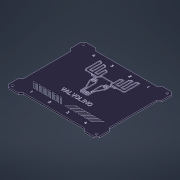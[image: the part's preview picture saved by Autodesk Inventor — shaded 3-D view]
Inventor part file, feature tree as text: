
AUTODESK INVENTOR PART (.ipt)
format: ipt  version: 2021.3 (Build 253353000, 353)  size: 1,772,032 bytes
history: native  units: mm
features: sketch x5, projected_geometry x4, extrude x2, mirror x2, chamfer x1, emboss x1, other x1, hole x1
ambient origin geometry x8: Origin, YZ Plane, XZ Plane, XY Plane, X Axis, Y Axis, Z Axis, Center Point
bodies: Solid1 (feature_tree)
feature tree (17):
  extrude  "Extrusion1"  Depth=110.0mm
  extrude  "Extrusion2"  Depth=2.0mm
  mirror  "Mirror1"
  chamfer  "Chamfer1"  Distance=2.0mm
  emboss  "Emboss1"
  other  "Grill1"
  mirror  "Mirror2"
  hole  "Hole1"  [1 undecoded]
  sketch  "Sketch1"  dims[d0=130.0mm d1=110.0mm]
  sketch  "Sketch2"  dims[d2=4.0mm d3=15.0mm d4=2.0mm d5=0.0mm]
  projected_geometry  "Projected Loop1"
  sketch  "Sketch3"  dims[d74=10.0mm d75=4.0mm]
  projected_geometry  "Projected Loop2"
  sketch  "Sketch4"  dims[d76=2.0mm]
  projected_geometry  "Projected Loop3"
  sketch  "Sketch5"  dims[d77=4.0mm d78=4.0mm d79=4.0mm d80=135.0deg d81=19.0mm d82=4.0mm d83=4.0mm d85=2.0mm d86=8.0mm d87=2.0mm d89=2.0mm d90=6.0mm d91=5.0mm d92=3.0mm d93=8.0mm d94=12.0mm d95=6.0mm d96=6.0mm d98=2.0mm d99=4.0mm d100=2.0mm d101=8.0mm d104=1.0mm d105=1.0mm d106=2.0mm d107=1.0mm d108=1.0mm d109=2.0mm d110=1.0mm d111=0.25mm d112=0.25mm d113=0.25mm d114=0.25mm d115=0.25mm d116=0.25mm d117=0.256mm d118=0.25mm d119=0.25mm d120=0.25mm d121=0.25mm d122=0.25mm d123=0.25mm d124=0.25mm d125=0.5mm d126=0.0mm d127=0.5mm d128=2.0mm d129=45.0deg d130=22.5mm d131=22.5mm d132=22.5mm d133=5.0mm d135=5.0mm d136=22.5mm d137=22.5mm d138=22.5mm d139=5.0mm d140=5.0mm d141=30.0mm d142=10.0mm d143=50.0mm d144=0.5mm d145=0.0mm d146=9.0mm d147=42.0mm d148=2.5mm d149=14.0mm d150=135.0deg d151=5.0mm d152=5.0mm d153=3.0mm d154=100.0mm d156=4.0mm d157=10.0mm d159=10.0mm d161=1.414214mm d162=2.0mm d163=0.0mm d164=1.0mm d165=2.0mm d166=0.0mm d167=1.414214mm d168=0.0mm d169=0.0mm d170=1.0mm d171=0.0mm d172=0.0mm d173=0.0mm d174=19.8mm d175=1.0mm d176=1.0mm d177=1.0mm d178=1.0mm d179=3.4mm d180=6.0mm d181=4.0mm d182=2.0mm d183=90.0deg d184=5.0mm d185=0.0mm]
  projected_geometry  "Projected Loop4"
note: 1 required parameter value undecoded (feature->parameter linkage not recoverable at this tier; creation-order binding heuristic only, values carry confidence <= 0.55)
